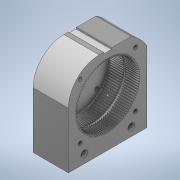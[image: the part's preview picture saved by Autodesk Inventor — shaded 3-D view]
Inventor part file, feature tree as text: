
AUTODESK INVENTOR PART (.ipt)
format: ipt  version: 2022 (Build 260153000, 153)  size: 1,537,024 bytes
history: mixed  units: mm
features: sketch x7, extrude x6, other x3, fillet x1, imported_body x1
ambient origin geometry x8: Origin, YZ Plane, XZ Plane, XY Plane, X Axis, Y Axis, Z Axis, Center Point
bodies: Solid1 (imported_parasolid)
feature tree (18):
  other  "Assembly2.iam"
  other  "96Gears_Stage_1_modified.ipt:1"
  other  "96Gears_Stage_2_modified.ipt:1"
  extrude  "Extrusion3"  Depth=3.0mm
  extrude  "Extrusion5"  Depth=1.0mm TaperAngle=0.0deg
  extrude  "Extrusion6"  Depth=6.0mm TaperAngle=0.0deg
  extrude  "Extrusion7"  TaperAngle=0.0deg  [1 undecoded]
  extrude  "Extrusion8"  Depth=3.5mm
  extrude  "Extrusion9"  Depth=5.0mm
  fillet  "Fillet3"  Radius=3.0mm
  sketch  "Sketch5"  dims[d7=6.0mm d8=1.0mm d9=0.0mm]
  sketch  "Sketch4"  dims[d0=10.0mm d6=3.0mm]
  sketch  "Sketch7"  dims[d17=32.25mm d18=6.0mm d19=0.0mm]
  sketch  "Sketch8"  dims[d20=10.0mm d21=0.0mm d22=0.0mm]
  sketch  "Sketch9"  dims[d23=6.75mm d27=3.5mm]
  sketch  "Sketch10"  dims[d28=0.0mm d29=0.0mm d30=5.0mm d31=3.0mm d32=0.0mm]
  sketch  "Sketch11"  dims[d35=5.5mm d36=3.0mm d37=0.0mm d45=23.5mm]
  imported_body  NMx_Import_Brep_tag  [imported B-rep: ~806 faces, bbox_mm=[27.0, 66.5, 60.0]]
note: 1 required parameter value undecoded (feature->parameter linkage not recoverable at this tier; creation-order binding heuristic only, values carry confidence <= 0.55)
